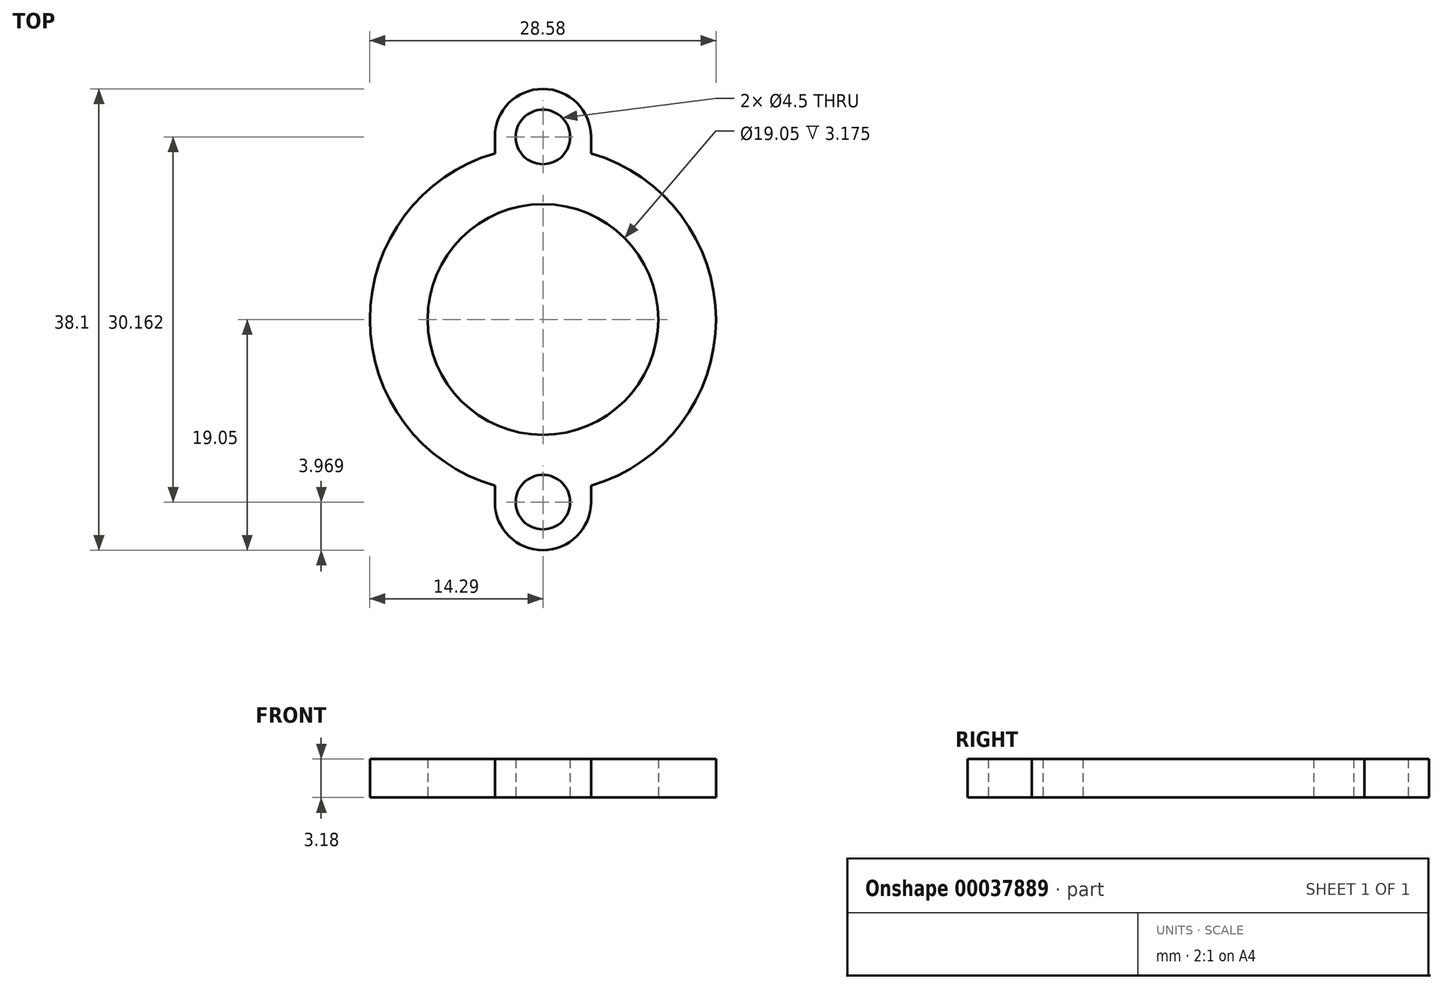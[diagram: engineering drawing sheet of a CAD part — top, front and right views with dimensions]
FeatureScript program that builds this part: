
annotation { "Feature Type Name" : "Feature", "Feature Type Description" : "" }
export const myFeature = defineFeature(function(context is Context, id is Id, definition is map)
    precondition{}
    {
        {
            var Q0;
            Q0=qCreatedBy(makeId("Top.planeOp"),FACE);
            var sketch = newSketch(context, id + "F0", { "sketchPlane" : qUnion([Q0])});
            skCircle(sketch, "E0", {"center": v(0, 0) * mm, "radius": 9.53 * mm});
            skArc(sketch, "E1", {"start": v(3.97, -13.73) * mm, "mid": v(14.29, 0) * mm, "end": v(3.97, 13.73) * mm});
            skArc(sketch, "E2", {"start": v(-3.97, 13.73) * mm, "mid": v(-14.29, 0) * mm, "end": v(-3.97, -13.73) * mm});
            skLineSegment(sketch, "E3", {"start": v(0, -15.08) * mm, "end": v(0, 15.08) * mm, "construction": true});
            skLineSegment(sketch, "E4", {"start": v(-3.97, 15.08) * mm, "end": v(3.97, 15.08) * mm, "construction": true});
            skLineSegment(sketch, "E5", {"start": v(-3.97, 15.08) * mm, "end": v(-3.97, 13.73) * mm});
            skLineSegment(sketch, "E6", {"start": v(3.97, 15.08) * mm, "end": v(3.97, 13.73) * mm});
            skLineSegment(sketch, "E7", {"start": v(-3.97, -15.08) * mm, "end": v(3.97, -15.08) * mm, "construction": true});
            skLineSegment(sketch, "E8", {"start": v(3.97, -15.08) * mm, "end": v(3.97, -13.73) * mm});
            skLineSegment(sketch, "E9", {"start": v(-3.97, -15.08) * mm, "end": v(-3.97, -13.73) * mm});
            skArc(sketch, "E10", {"start": v(3.97, 15.08) * mm, "mid": v(0, 19.05) * mm, "end": v(-3.97, 15.08) * mm});
            skArc(sketch, "E11", {"start": v(-3.97, -15.08) * mm, "mid": v(0, -19.05) * mm, "end": v(3.97, -15.08) * mm});
            skCircle(sketch, "E12", {"center": v(0, 15.08) * mm, "radius": 2.25 * mm});
            skCircle(sketch, "E13", {"center": v(0, -15.08) * mm, "radius": 2.25 * mm});
            skSolve(sketch);
        }
        {
            var Q0;
            Q0 = qSketchRegion(id + "F0", true);
            extrude(context, id + "F1", {"entities" : qUnion([Q0]), "depth" : 3.17 * mm});
        }
    });
